FCSTD DOCUMENT  (FreeCAD 0.19R)
Label: layout
License: All rights reserved
LicenseURL: http://en.wikipedia.org/wiki/All_rights_reserved
objects: Sketcher::SketchObject×2, PartDesign::Body×1
note: 3 computed .brp shape members not serialized (recipe doc carries the construction recipe); baked Part::Feature solids carry a one-line shape summary decoded from their .brp

FEATURE [Sketcher::SketchObject] Sketch
  FullyConstrained = true
  MapMode = 5
  Support = -> [XY_Plane]
  sketch-geometry (4):
    g0: LineSegment StartX=-20 StartY=25 StartZ=0 EndX=20 EndY=25 EndZ=0
    g1: LineSegment StartX=20 StartY=25 StartZ=0 EndX=20 EndY=-25 EndZ=0
    g2: LineSegment StartX=20 StartY=-25 StartZ=0 EndX=-20 EndY=-25 EndZ=0
    g3: LineSegment StartX=-20 StartY=-25 StartZ=0 EndX=-20 EndY=25 EndZ=0
  constraints (11):
    c: Coincident(g0,g1)
    c: Coincident(g1,g2)
    c: Coincident(g2,g3)
    c: Coincident(g3,g0)
    c: Horizontal(g0)
    c: Horizontal(g2)
    c: Vertical(g1)
    c: Vertical(g3)
    c: Symmetric(g0,g1,g-1)
    c: Distance(g0) = 40
    c: Distance(g1) = 50
FEATURE [Sketcher::SketchObject] Sketch001
  ExternalGeometry = -> [Sketch]
  FullyConstrained = true
  MapMode = 5
  Support = -> [XY_Plane]
  sketch-geometry (12):
    g0: LineSegment StartX=-15 StartY=30 StartZ=0 EndX=15 EndY=30 EndZ=0
    g1: LineSegment StartX=22.5 StartY=22.5 StartZ=0 EndX=22.5 EndY=-17.5 EndZ=0
    g2: LineSegment StartX=15 StartY=-25 StartZ=0 EndX=-15 EndY=-25 EndZ=0
    g3: LineSegment StartX=-22.5 StartY=-17.5 StartZ=0 EndX=-22.5 EndY=22.5 EndZ=0
    g4: ArcOfCircle CenterX=-15 CenterY=22.5 CenterZ=0 NormalX=0 NormalY=0 NormalZ=1 AngleXU=0 Radius=7.5 StartAngle=1.5708 EndAngle=3.14159
    g5: ArcOfCircle CenterX=15 CenterY=22.5 CenterZ=0 NormalX=0 NormalY=0 NormalZ=1 AngleXU=0 Radius=7.5 StartAngle=0 EndAngle=1.5708
    g6: ArcOfCircle CenterX=15 CenterY=-17.5 CenterZ=0 NormalX=0 NormalY=0 NormalZ=1 AngleXU=0 Radius=7.5 StartAngle=4.71239 EndAngle=6.28319
    g7: ArcOfCircle CenterX=-15 CenterY=-17.5 CenterZ=0 NormalX=0 NormalY=0 NormalZ=1 AngleXU=0 Radius=7.5 StartAngle=3.14159 EndAngle=4.71239
    g8: LineSegment StartX=-18 StartY=25.7 StartZ=0 EndX=18 EndY=25.7 EndZ=0
    g9: LineSegment StartX=18 StartY=25.7 StartZ=0 EndX=18 EndY=-20.8 EndZ=0
    g10: LineSegment StartX=18 StartY=-20.8 StartZ=0 EndX=-18 EndY=-20.8 EndZ=0
    g11: LineSegment StartX=-18 StartY=-20.8 StartZ=0 EndX=-18 EndY=25.7 EndZ=0
  constraints (30):
    c: Horizontal(g2)
    c: Vertical(g1)
    c: Vertical(g3)
    c: Tangent(g0,g4) = 1.5708
    c: Tangent(g3,g4) = 1.5708
    c: Tangent(g0,g5) = 1.5708
    c: Tangent(g1,g5) = 1.5708
    c: Tangent(g1,g6) = 1.5708
    c: Tangent(g2,g6) = 1.5708
    c: Tangent(g2,g7) = 1.5708
    c: Tangent(g3,g7) = 1.5708
    c: Equal(g6,g5)
    c: Equal(g5,g4)
    c: Equal(g4,g7)
    c: PointOnObject(g2,g-3)
    c: Diameter(g7) = 15
    c: Symmetric(g0,g0,g-2)
    c: DistanceY(g0) = 30
    c: DistanceX(g0) = -15
    c: Coincident(g8,g9)
    c: Coincident(g9,g10)
    c: Coincident(g10,g11)
    c: Coincident(g11,g8)
    c: Horizontal(g10)
    c: Vertical(g9)
    c: Vertical(g11)
    c: Symmetric(g8,g8,g-2)
    c: DistanceY(g8) = 25.7
    c: Distance(g8) = 36
    c: DistanceY(g10) = -20.8
FEATURE [PartDesign::Body] Body
  Group = -> [Sketch,Sketch001]
  Origin = -> Origin
